# Revit family: equip-water-cooler-elkay-EHWM217C
name_source: partatom
category: Plumbing Fixtures
units: mm (PartAtom-declared; Revit-internal decimal feet)

## family parameters
Always vertical = Yes
Cut with Voids When Loaded = No
OmniClass Number = 23.45.00.00
OmniClass Title = Sanitary, Laundry, and Cleaning Equipment
Part Type = Normal
Room Calculation Point = No
Round Connector Dimension = Use Radius
Shared = No
Work Plane-Based = No

## types (1)
- EHWM217C
    Activation = Push Button
    Basin Material = Metal - Steel - Stainless - Chrome
    Bubbler = Vandal-Resistant
    Button Material = Metal - Steel - Stainless - Chrome
    CW Connection = Yes
    Chiller = NA (Non-Refrigerated)
    Cooler Depth = 1' - 6 5/8"
    Cooler Separation = 0' - 6 5/8"
    Cooler Width = 1' - 0 1/8"
    Description = Water Cooler
    Dispenser Height = 2' - 9"
    Fountain = EHWM
    Glass Filter = -
    HW Connection = No
    Lower Cooler Rim Height = 2' - 9 1/2"
    Lower Orifice Height = 2' - 11 1/8"
    Manufacturer = Elkay
    Model = EHWM217C
    Mounting = Wall Moun (On-Wall)
    Orifice to Rim = 0' - 1 5/8"
    Panel Material = Metal - Steel - Stainless - Chrome
    Rim to Dispenser = 0' - 6 1/2"
    Type = Double (Two Station)
    URL = http://www.elkay.com
    Upper Cooler Depth = 1' - 0 7/8"
    Upper Cooler Rim Height = 3' - 3 1/2"
    Upper Orifice Height = 3' - 5 1/8"
    Upper Rim Height = 3' - 3 1/2"
    Vent Connection = No
    Version = 1.0.0.0
    Wall Plate Material = Metal - Steel - Stainless - Chrome
    Waste Connection = Yes
    Water Service Flow = 0 GPM
    Water Service Size Radius = 0' - 0 1/4"

## geometry (parser evidence)
native form markers: Sweep x9
no freeform markers — native parametric forms only
